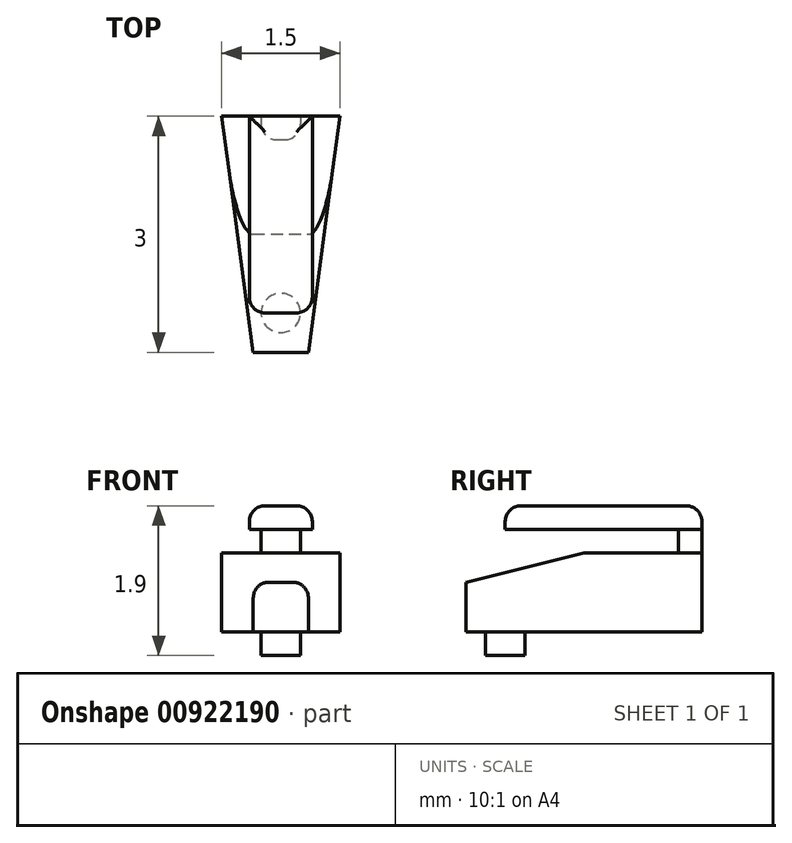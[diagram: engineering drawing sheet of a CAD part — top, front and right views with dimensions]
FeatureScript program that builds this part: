
annotation { "Feature Type Name" : "Feature", "Feature Type Description" : "" }
export const myFeature = defineFeature(function(context is Context, id is Id, definition is map)
    precondition{}
    {
        {
            var Q0;
            Q0=qCreatedBy(makeId("Front.planeOp"),FACE);
            var sketch = newSketch(context, id + "F0", { "sketchPlane" : qUnion([Q0])});
            skLineSegment(sketch, "E0.bottom", {"start": v(0, 0) * mm, "end": v(1.5, 0) * mm});
            skLineSegment(sketch, "E0.top", {"start": v(0, 1) * mm, "end": v(1.5, 1) * mm});
            skLineSegment(sketch, "E0.left", {"start": v(0, 0) * mm, "end": v(0, 1) * mm});
            skLineSegment(sketch, "E0.right", {"start": v(1.5, 0) * mm, "end": v(1.5, 1) * mm});
            skSolve(sketch);
        }
        {
            var Q0;
            Q0=makeQuery(id+"F0.imprint","IMPRINT",FACE,{"disambiguationData":[TD([[makeQuery(id+"F0.imprint","IMPRINT",EDGE,{"derivedFrom":sQuery(id+"F0.wireOp",EDGE,"E0.bottom")}),1.0]])]});
            extrude(context, id + "F1", {"entities" : qUnion([Q0]), "depth" : 3 * mm, "offsetDistance" : 25 * mm});
        }
        {
            var Q0;
            Q0=makeQuery(id+"F1.opExtrude","SWEPT_FACE",FACE,{"disambiguationData":[OSD([sQuery(id+"F0.wireOp",EDGE,"E0.right")])]});
            var sketch = newSketch(context, id + "F2", { "sketchPlane" : qUnion([Q0])});
            skLineSegment(sketch, "E1", {"start": v(-3, 0.63) * mm, "end": v(-1.5, 1) * mm});
            skLineSegment(sketch, "E2", {"start": v(-1.5, 1) * mm, "end": v(-3, 1) * mm});
            skLineSegment(sketch, "E3", {"start": v(-3, 1) * mm, "end": v(-3, 0.63) * mm});
            skSolve(sketch);
        }
        {
            var Q0;
            Q0=makeQuery(id+"F2.imprint","IMPRINT",FACE,{"disambiguationData":[TD([[makeQuery(id+"F2.imprint","IMPRINT",EDGE,{"derivedFrom":sQuery(id+"F2.wireOp",EDGE,"E1")}),1.0]])]});
            extrude(context, id + "F3", {"entities" : qUnion([Q0]), "operationType" : NewBodyOperationType.REMOVE, "oppositeDirection" : true, "depth" : 25 * mm, "offsetDistance" : 25 * mm});
        }
        {
            var Q0;
            Q0=makeQuery(id+"F1.opExtrude","SWEPT_FACE",FACE,{"disambiguationData":[OSD([sQuery(id+"F0.wireOp",EDGE,"E0.top")])]});
            var sketch = newSketch(context, id + "F4", { "sketchPlane" : qUnion([Q0])});
            skLineSegment(sketch, "E4", {"start": v(0, 0) * mm, "end": v(0.4, -3) * mm});
            skLineSegment(sketch, "E5", {"start": v(0.4, -3) * mm, "end": v(1.1, -3) * mm});
            skLineSegment(sketch, "E6", {"start": v(1.1, -3) * mm, "end": v(1.5, 0) * mm});
            skLineSegment(sketch, "E7.0.0", {"start": v(0, -1.5) * mm, "end": v(0, -3) * mm});
            skLineSegment(sketch, "E7.0.1", {"start": v(0, -3) * mm, "end": v(1.5, -3) * mm});
            skLineSegment(sketch, "E7.0.2", {"start": v(1.5, -3) * mm, "end": v(1.5, -1.5) * mm});
            skLineSegment(sketch, "E7.0.3", {"start": v(1.5, -1.5) * mm, "end": v(0, -1.5) * mm});
            skSolve(sketch);
        }
        {
            var Q0;
            {var subQ1=sQuery(id+"F0.wireOp",EDGE,"E0.top");var subQ2=makeQuery(id+"F1.opExtrude","SWEPT_EDGE",EDGE,{"disambiguationData":[OSD([subQ1,sQuery(id+"F0.wireOp",EDGE,"E0.right")])]});Q0=makeQuery(id+"F4.imprint","IMPRINT",FACE,{"disambiguationData":[TD([[makeQuery(id+"F4.imprint","IMPRINT",EDGE,{"derivedFrom":subQ2}),1.0]])]});}
            var Q1;
            {var subQ5=sQuery(id+"F4.wireOp",EDGE,"E7.0.2");Q1=makeQuery(id+"F4.imprint","IMPRINT",FACE,{"disambiguationData":[TD([[makeQuery(id+"F4.imprint","IMPRINT",EDGE,{"derivedFrom":subQ5}),1.0]])]});}
            var Q2;
            {var subQ1=sQuery(id+"F0.wireOp",EDGE,"E0.top");var subQ2=makeQuery(id+"F1.opExtrude","SWEPT_EDGE",EDGE,{"disambiguationData":[OSD([subQ1,sQuery(id+"F0.wireOp",EDGE,"E0.left")])]});Q2=makeQuery(id+"F4.imprint","IMPRINT",FACE,{"disambiguationData":[TD([[makeQuery(id+"F4.imprint","IMPRINT",EDGE,{"derivedFrom":subQ2}),-1.0]])]});}
            var Q3;
            {var subQ5=sQuery(id+"F4.wireOp",EDGE,"E7.0.0");Q3=makeQuery(id+"F4.imprint","IMPRINT",FACE,{"disambiguationData":[TD([[makeQuery(id+"F4.imprint","IMPRINT",EDGE,{"derivedFrom":subQ5}),1.0]])]});}
            extrude(context, id + "F5", {"entities" : qUnion([Q0, Q1, Q2, Q3]), "operationType" : NewBodyOperationType.REMOVE, "oppositeDirection" : true, "depth" : 25 * mm, "offsetDistance" : 25 * mm});
        }
        {
            var Q0;
            Q0=makeQuery(id+"F1.opExtrude","SWEPT_FACE",FACE,{"disambiguationData":[OSD([sQuery(id+"F0.wireOp",EDGE,"E0.bottom")])]});
            var sketch = newSketch(context, id + "F6", { "sketchPlane" : qUnion([Q0])});
            skCircle(sketch, "E8", {"center": v(0.75, 2.5) * mm, "radius": 0.25 * mm});
            skPoint(sketch, "E8.centerSnap0", {"position": v(0.75, 3) * mm});
            skSolve(sketch);
        }
        {
            var Q0;
            Q0=makeQuery(id+"F6.imprint","IMPRINT",FACE,{"disambiguationData":[TD([[makeQuery(id+"F6.imprint","IMPRINT",EDGE,{"derivedFrom":sQuery(id+"F6.wireOp",EDGE,"E8")}),1.0]])]});
            extrude(context, id + "F7", {"entities" : qUnion([Q0]), "operationType" : NewBodyOperationType.ADD, "depth" : 0.3 * mm, "offsetDistance" : 25 * mm});
        }
        {
            var Q0;
            Q0=makeQuery(id+"F1.opExtrude","SWEPT_FACE",FACE,{"disambiguationData":[OSD([sQuery(id+"F0.wireOp",EDGE,"E0.top")])]});
            var sketch = newSketch(context, id + "F8", { "sketchPlane" : qUnion([Q0])});
            skLineSegment(sketch, "E9.bottom", {"start": v(0.5, 0) * mm, "end": v(1, 0) * mm});
            skLineSegment(sketch, "E9.top", {"start": v(0.5, -0.3) * mm, "end": v(1, -0.3) * mm});
            skLineSegment(sketch, "E9.left", {"start": v(0.5, 0) * mm, "end": v(0.5, -0.3) * mm});
            skLineSegment(sketch, "E9.right", {"start": v(1, 0) * mm, "end": v(1, -0.3) * mm});
            skSolve(sketch);
        }
        {
            var Q0;
            Q0=makeQuery(id+"F8.imprint","IMPRINT",FACE,{"disambiguationData":[TD([[makeQuery(id+"F8.imprint","IMPRINT",EDGE,{"derivedFrom":sQuery(id+"F8.wireOp",EDGE,"E9.bottom")}),-1.0]])]});
            extrude(context, id + "F9", {"entities" : qUnion([Q0]), "operationType" : NewBodyOperationType.ADD, "depth" : 0.3 * mm, "offsetDistance" : 25 * mm});
        }
        {
            var Q0;
            Q0=makeQuery(id+"F9.opExtrude","CAP_FACE",FACE,{"disambiguationData":[OSD([sQuery(id+"F8.wireOp",EDGE,"E9.bottom"),sQuery(id+"F8.wireOp",EDGE,"E9.top"),sQuery(id+"F8.wireOp",EDGE,"E9.left"),sQuery(id+"F8.wireOp",EDGE,"E9.right")])],"isStart":false});
            var sketch = newSketch(context, id + "F10", { "sketchPlane" : qUnion([Q0])});
            skLineSegment(sketch, "E10.bottom", {"start": v(0.35, 0) * mm, "end": v(1.15, 0) * mm});
            skLineSegment(sketch, "E10.top", {"start": v(0.35, -2.5) * mm, "end": v(1.15, -2.5) * mm});
            skLineSegment(sketch, "E10.left", {"start": v(0.35, 0) * mm, "end": v(0.35, -2.5) * mm});
            skLineSegment(sketch, "E10.right", {"start": v(1.15, 0) * mm, "end": v(1.15, -2.5) * mm});
            skSolve(sketch);
        }
        {
            var Q0;
            Q0=makeQuery(id+"F10.imprint","IMPRINT",FACE,{"disambiguationData":[TD([[makeQuery(id+"F10.imprint","IMPRINT",EDGE,{"derivedFrom":sQuery(id+"F10.wireOp",EDGE,"E10.top")}),1.0]])]});
            var Q1;
            Q1=makeQuery(id+"F10.imprint","IMPRINT",FACE,{"disambiguationData":[TD([[makeQuery(id+"F10.imprint","IMPRINT",EDGE,{"derivedFrom":makeQuery(id+"F9.opExtrude","CAP_EDGE",EDGE,{"disambiguationData":[OSD([sQuery(id+"F8.wireOp",EDGE,"E9.top")])],"isStart":false})}),1.0]])]});
            extrude(context, id + "F11", {"entities" : qUnion([Q0, Q1]), "operationType" : NewBodyOperationType.ADD, "depth" : 0.3 * mm, "offsetDistance" : 25 * mm});
        }
        {
            var Q0;
            Q0=makeQuery(id+"F5.boolean.opBoolean","INTERSECT",EDGE,{"derivedFrom":[makeQuery(id+"F3.boolean.opBoolean","COPY",FACE,{"derivedFrom":makeQuery(id+"F3.opExtrude","SWEPT_FACE",FACE,{"disambiguationData":[OSD([sQuery(id+"F2.wireOp",EDGE,"E1")])]})}),makeQuery(id+"F5.opExtrude","SWEPT_FACE",FACE,{"disambiguationData":[OSD([sQuery(id+"F4.wireOp",EDGE,"E6")])]})]});
            var Q1;
            Q1=makeQuery(id+"F5.boolean.opBoolean","INTERSECT",EDGE,{"derivedFrom":[makeQuery(id+"F3.boolean.opBoolean","COPY",FACE,{"derivedFrom":makeQuery(id+"F3.opExtrude","SWEPT_FACE",FACE,{"disambiguationData":[OSD([sQuery(id+"F2.wireOp",EDGE,"E1")])]})}),makeQuery(id+"F5.opExtrude","SWEPT_FACE",FACE,{"disambiguationData":[OSD([sQuery(id+"F4.wireOp",EDGE,"E4")])]})]});
            var Q2;
            Q2=makeQuery(id+"F3.boolean.opBoolean","COPY",EDGE,{"derivedFrom":makeQuery(id+"F3.opExtrude","SWEPT_EDGE",EDGE,{"disambiguationData":[OSD([sQuery(id+"F0.wireOp",EDGE,"E0.right"),sQuery(id+"F2.wireOp",EDGE,"E1"),sQuery(id+"F2.wireOp",EDGE,"E3")])]})});
            var Q3;
            Q3=makeQuery(id+"F5.boolean.opBoolean","COPY",EDGE,{"derivedFrom":makeQuery(id+"F5.opExtrude","CAP_EDGE",EDGE,{"disambiguationData":[OSD([sQuery(id+"F4.wireOp",EDGE,"E6")])],"isStart":true})});
            var Q4;
            Q4=makeQuery(id+"F5.boolean.opBoolean","COPY",EDGE,{"derivedFrom":makeQuery(id+"F5.opExtrude","CAP_EDGE",EDGE,{"disambiguationData":[OSD([sQuery(id+"F4.wireOp",EDGE,"E4")])],"isStart":true})});
            var Q5;
            Q5=makeQuery(id+"F5.boolean.opBoolean","COPY",EDGE,{"derivedFrom":makeQuery(id+"F5.opExtrude","SWEPT_EDGE",EDGE,{"disambiguationData":[OSD([sQuery(id+"F4.wireOp",EDGE,"E4"),sQuery(id+"F4.wireOp",EDGE,"E7.0.1")])]})});
            var Q6;
            Q6=makeQuery(id+"F5.boolean.opBoolean","COPY",EDGE,{"derivedFrom":makeQuery(id+"F5.opExtrude","SWEPT_EDGE",EDGE,{"disambiguationData":[OSD([sQuery(id+"F4.wireOp",EDGE,"E6"),sQuery(id+"F4.wireOp",EDGE,"E7.0.1")])]})});
            fillet(context, id + "F12", {"entities" : qUnion([Q0, Q1, Q2, Q3, Q4, Q5, Q6]), "radius" : 0.2 * mm, "tangentPropagation" : true, "allowEdgeOverflow" : false});
        }
        {
            var Q0;
            Q0=makeQuery(id+"F9.opExtrude","SWEPT_EDGE",EDGE,{"disambiguationData":[OSD([sQuery(id+"F8.wireOp",EDGE,"E9.top"),sQuery(id+"F8.wireOp",EDGE,"E9.right")])]});
            var Q1;
            Q1=makeQuery(id+"F9.opExtrude","SWEPT_EDGE",EDGE,{"disambiguationData":[OSD([sQuery(id+"F8.wireOp",EDGE,"E9.top"),sQuery(id+"F8.wireOp",EDGE,"E9.left")])]});
            var Q2;
            Q2=makeQuery(id+"F11.opExtrude","SWEPT_EDGE",EDGE,{"disambiguationData":[OSD([sQuery(id+"F10.wireOp",EDGE,"E10.top"),sQuery(id+"F10.wireOp",EDGE,"E10.left")])]});
            var Q3;
            Q3=makeQuery(id+"F11.opExtrude","SWEPT_EDGE",EDGE,{"disambiguationData":[OSD([sQuery(id+"F10.wireOp",EDGE,"E10.top"),sQuery(id+"F10.wireOp",EDGE,"E10.right")])]});
            var Q4;
            Q4=makeQuery(id+"F11.opExtrude","CAP_EDGE",EDGE,{"disambiguationData":[OSD([sQuery(id+"F10.wireOp",EDGE,"E10.top")])],"isStart":false});
            var Q5;
            Q5=makeQuery(id+"F11.opExtrude","CAP_EDGE",EDGE,{"disambiguationData":[OSD([sQuery(id+"F10.wireOp",EDGE,"E10.left")])],"isStart":false});
            var Q6;
            Q6=makeQuery(id+"F11.opExtrude","CAP_FACE",FACE,{"disambiguationData":[OSD([sQuery(id+"F10.wireOp",EDGE,"E10.bottom"),sQuery(id+"F10.wireOp",EDGE,"E10.top"),sQuery(id+"F10.wireOp",EDGE,"E10.left"),sQuery(id+"F10.wireOp",EDGE,"E10.right")])],"isStart":false});
            fillet(context, id + "F13", {"entities" : qUnion([Q0, Q1, Q2, Q3, Q4, Q5, Q6]), "radius" : 0.2 * mm, "tangentPropagation" : true, "allowEdgeOverflow" : false});
        }
    });
